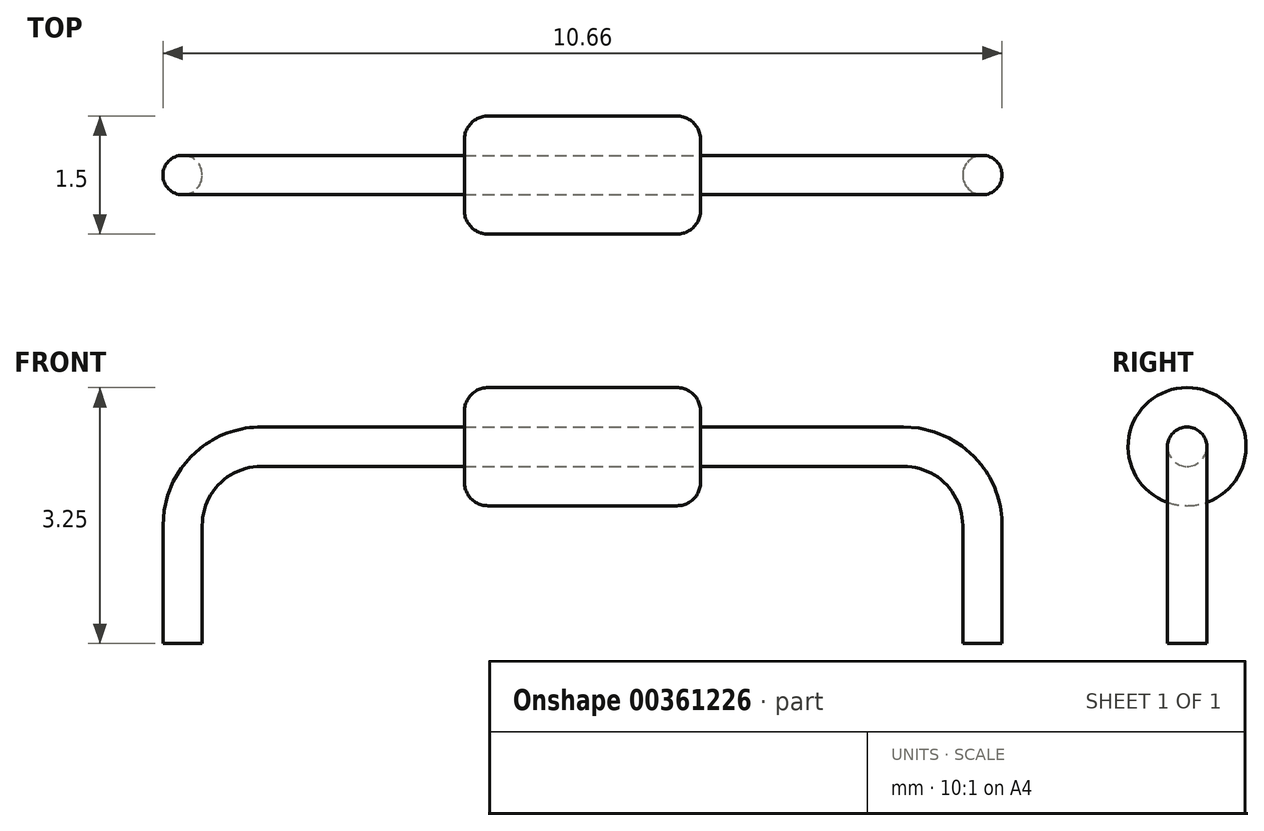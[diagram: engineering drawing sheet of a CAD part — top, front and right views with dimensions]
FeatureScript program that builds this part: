
annotation { "Feature Type Name" : "Feature", "Feature Type Description" : "" }
export const myFeature = defineFeature(function(context is Context, id is Id, definition is map)
    precondition{}
    {
        {
            var Q0;
            Q0=qCreatedBy(makeId("Right.planeOp"),FACE);
            var sketch = newSketch(context, id + "F0", { "sketchPlane" : qUnion([Q0])});
            skCircle(sketch, "E0", {"center": v(0, 0) * mm, "radius": 0.75 * mm});
            skSolve(sketch);
        }
        {
            var Q0;
            Q0=qSketchRegion(id+"F0",true);
            extrude(context, id + "F1", {"entities" : qUnion([Q0]), "depth" : 3 * mm, "symmetric" : true});
        }
        {
            var Q0;
            Q0=makeQuery(id+"F1.opExtrude","CAP_EDGE",EDGE,{"disambiguationData":[OSD([sQuery(id+"F0.wireOp",EDGE,"E0")])],"isStart":true});
            var Q1;
            Q1=makeQuery(id+"F1.opExtrude","CAP_EDGE",EDGE,{"disambiguationData":[OSD([sQuery(id+"F0.wireOp",EDGE,"E0")])],"isStart":false});
            fillet(context, id + "F2", {"entities" : qUnion([Q0, Q1]), "radius" : 0.3 * mm, "tangentPropagation" : true, "allowEdgeOverflow" : false});
        }
        {
            var Q0;
            Q0=qCreatedBy(makeId("Front.planeOp"),FACE);
            var sketch = newSketch(context, id + "F3", { "sketchPlane" : qUnion([Q0])});
            skLineSegment(sketch, "E1", {"start": v(-5.08, -2.5) * mm, "end": v(-5.08, -1) * mm});
            skLineSegment(sketch, "E2", {"start": v(-4.08, 0) * mm, "end": v(4.08, 0) * mm});
            skLineSegment(sketch, "E3", {"start": v(5.08, -1) * mm, "end": v(5.08, -2.5) * mm});
            skPoint(sketch, "E4.visualSharp", {"position": v(-5.08, 0) * mm});
            skArc(sketch, "E4.filletArc", {"start": v(-4.08, 0) * mm, "mid": v(-4.79, -0.3) * mm, "end": v(-5.08, -1) * mm});
            skPoint(sketch, "E5.visualSharp", {"position": v(5.08, 0) * mm});
            skArc(sketch, "E5.filletArc", {"start": v(5.08, -1) * mm, "mid": v(4.79, -0.3) * mm, "end": v(4.08, 0) * mm});
            skPoint(sketch, "E6", {"position": v(0, 0) * mm});
            skSolve(sketch);
        }
        {
            var Q0;
            Q0=sQuery(id+"F3.wireOp",EDGE,"E1");
            var Q1;
            Q1=sQuery(id+"F3.wireOp",VERTEX,"E1.start");
            cPlane(context, id + "F4", {"entities" : qUnion([Q0, Q1]), "cplaneType" : CPlaneType.CURVE_POINT, "offset" : 25 * mm, "width" : 150 * mm, "height" : 150 * mm});
        }
        {
            var Q0;
            Q0=qCreatedBy(id+"F4.planeOp",FACE);
            var sketch = newSketch(context, id + "F5", { "sketchPlane" : qUnion([Q0])});
            skCircle(sketch, "E7", {"center": v(-5.08, 0) * mm, "radius": 0.25 * mm});
            skSolve(sketch);
        }
        {
            var Q0;
            Q0=qSketchRegion(id+"F5",true);
            var Q1;
            Q1=qConstructionFilter(qBodyType(qCreatedBy(id+"F3",EDGE),BodyType.WIRE),ConstructionObject.NO);
            sweep(context, id + "F6", {"profiles" : qUnion([Q0]), "path" : qUnion([Q1])});
        }
    });
